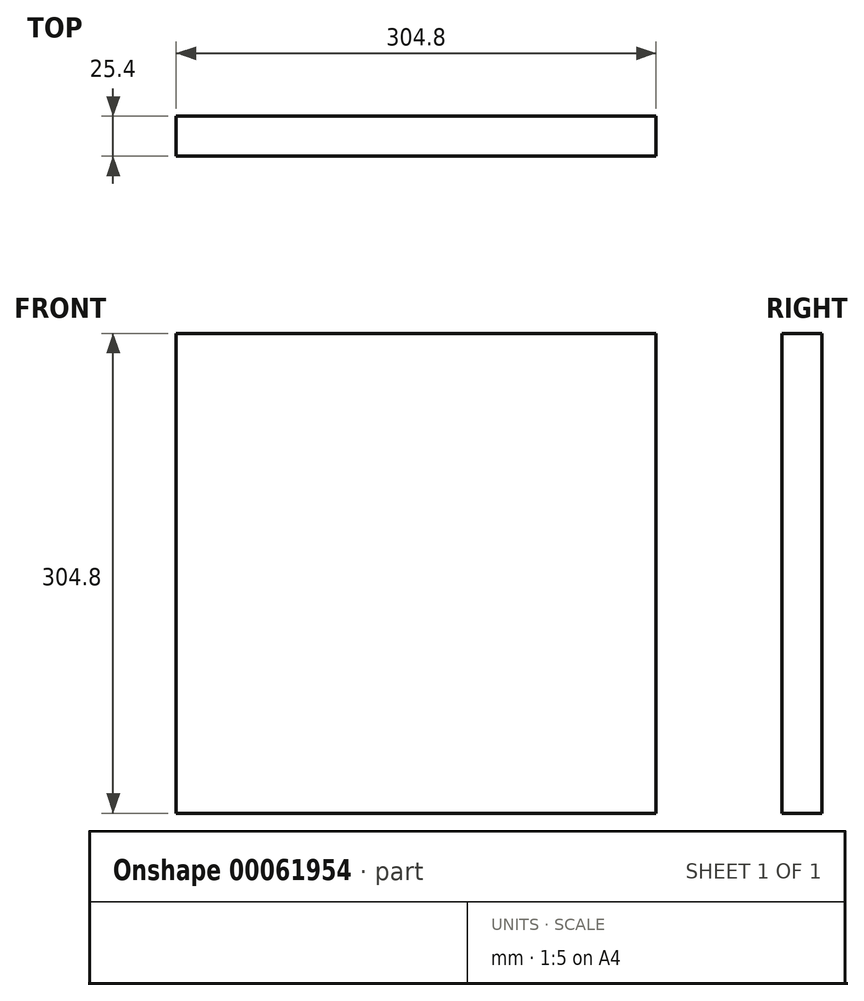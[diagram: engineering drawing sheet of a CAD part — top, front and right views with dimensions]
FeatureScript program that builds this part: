
annotation { "Feature Type Name" : "Feature", "Feature Type Description" : "" }
export const myFeature = defineFeature(function(context is Context, id is Id, definition is map)
    precondition{}
    {
        {
            var Q0;
            Q0=qCreatedBy(makeId("Front.planeOp"),FACE);
            var sketch = newSketch(context, id + "F0", { "sketchPlane" : qUnion([Q0])});
            skLineSegment(sketch, "E0.rect.bottom", {"start": v(152.4, -152.4) * mm, "end": v(-152.4, -152.4) * mm});
            skLineSegment(sketch, "E0.rect.top", {"start": v(152.4, 152.4) * mm, "end": v(-152.4, 152.4) * mm});
            skLineSegment(sketch, "E0.rect.left", {"start": v(152.4, -152.4) * mm, "end": v(152.4, 152.4) * mm});
            skLineSegment(sketch, "E0.rect.right", {"start": v(-152.4, -152.4) * mm, "end": v(-152.4, 152.4) * mm});
            skPoint(sketch, "E0.rect.middle", {"position": v(0, 0) * mm});
            skSolve(sketch);
        }
        {
            var Q0;
            Q0=makeQuery(id+"F0.imprint","IMPRINT",FACE,{"disambiguationData":[TD([[makeQuery(id+"F0.imprint","IMPRINT",EDGE,{"derivedFrom":sQuery(id+"F0.wireOp",EDGE,"E0.rect.bottom")}),-1.0]])]});
            extrude(context, id + "F1", {"entities" : qUnion([Q0]), "oppositeDirection" : true, "depth" : 25.4 * mm});
        }
    });
